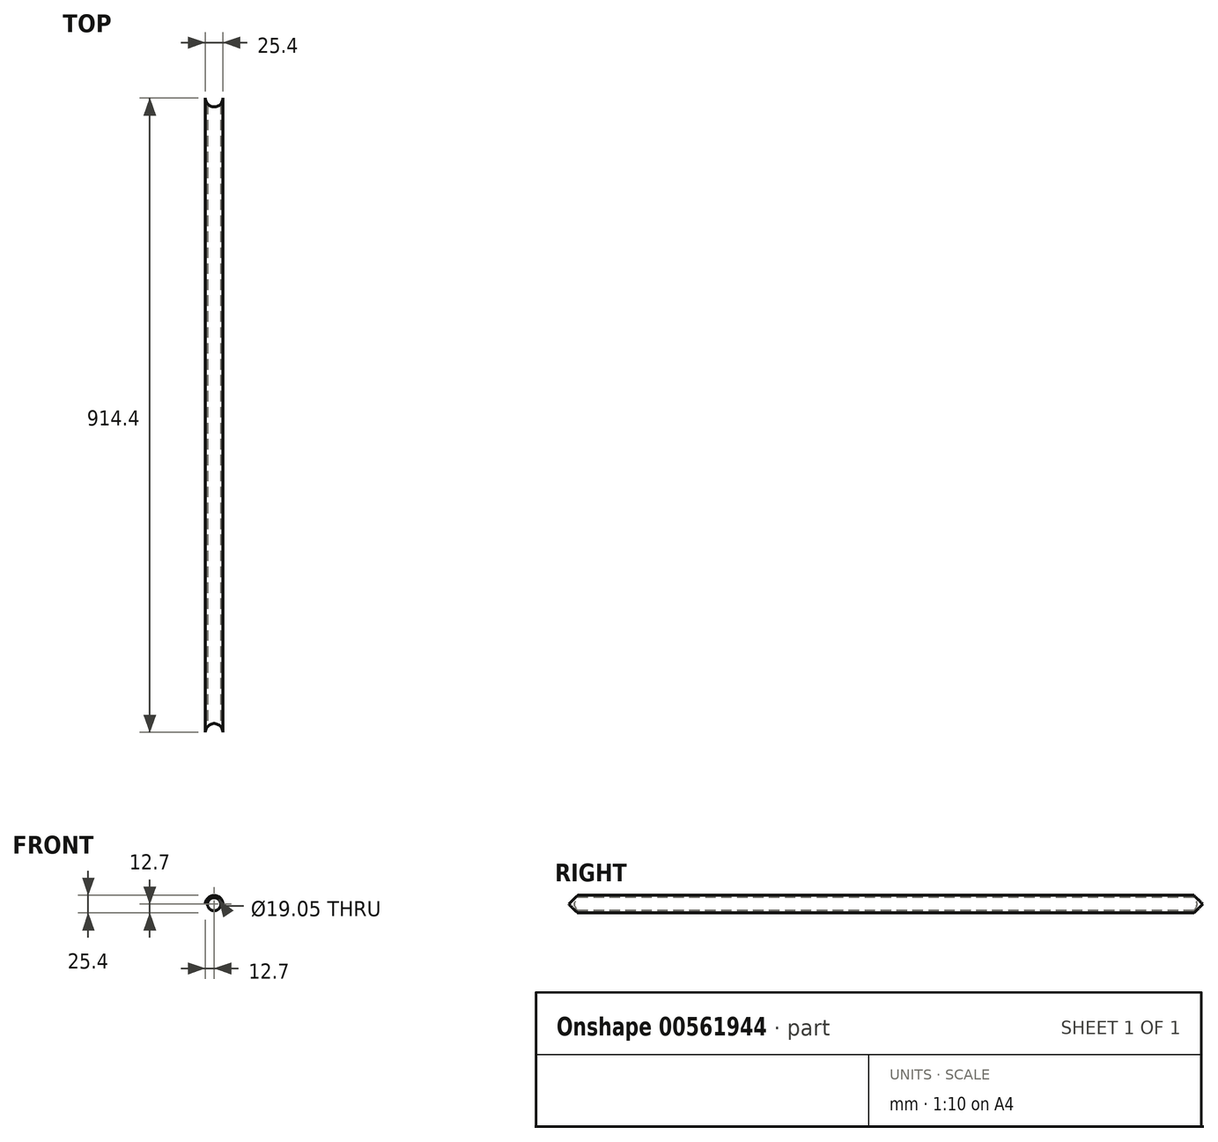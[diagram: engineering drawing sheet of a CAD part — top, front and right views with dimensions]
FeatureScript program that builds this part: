
annotation { "Feature Type Name" : "Feature", "Feature Type Description" : "" }
export const myFeature = defineFeature(function(context is Context, id is Id, definition is map)
    precondition{}
    {
        {
            var Q0;
            Q0=qCreatedBy(makeId("Front.planeOp"),FACE);
            var sketch = newSketch(context, id + "F0", { "sketchPlane" : qUnion([Q0])});
            skCircle(sketch, "E0", {"center": v(0, 0) * mm, "radius": 12.7 * mm});
            skCircle(sketch, "E1", {"center": v(0, 0) * mm, "radius": 9.53 * mm});
            skSolve(sketch);
        }
        {
            var Q0;
            Q0 = qSketchRegion(id + "F0", true);
            extrude(context, id + "F1", {"entities" : qUnion([Q0]), "oppositeDirection" : true, "depth" : 914.4 * mm, "offsetDistance" : 25.4 * mm, "symmetric" : true});
        }
        {
            var Q0;
            Q0=qCreatedBy(makeId("Top.planeOp"),FACE);
            var sketch = newSketch(context, id + "F2", { "sketchPlane" : qUnion([Q0])});
            skCircle(sketch, "E2", {"center": v(0, -457.2) * mm, "radius": 12.7 * mm});
            skCircle(sketch, "E3", {"center": v(0, 457.2) * mm, "radius": 12.7 * mm});
            skSolve(sketch);
        }
        {
            var Q0;
            Q0 = qSketchRegion(id + "F2", true);
            extrude(context, id + "F3", {"entities" : qUnion([Q0]), "operationType" : NewBodyOperationType.REMOVE, "depth" : 25.4 * mm, "offsetDistance" : 25.4 * mm, "symmetric" : true});
        }
    });
